# Revit family: Vents_TT PRO EC_2016_19.08
name_source: partatom
category: Оборудование
revit_build: Autodesk Revit 2016 (Build: 20160314_0715(x64)
units: mm (PartAtom-declared; Revit-internal decimal feet)

## family parameters
Всегда вертикально = Нет
На основе рабочей плоскости = Нет
Общий = Нет
При загрузке вырезать с полостями = Нет
Размер круглого соединителя = Использовать диаметр
Тип детали = Вставляется
Точка расчета площади = Нет

## types (7) — shared parameters
CAT0 = Да
CAT1 = Да
CAT2 = Да
Certification = by Manifacturer
EC motor = Да
Ingress Protection Rating = IPX4
LL7 = 98 мм
Motor IP Rating = IPX4
R3 = 49 мм
RR4 = 12 мм
URL = https://ventilation-system.com
Variable Speed Drive = Нет
Voltage = 230 В
W = 500 мм
Группа модели = ТТ PRO EC
Изготовитель = VENTS
Описание = Inline mixed-flow fan
Угол = 60.00°

## per-type parameters (varying)
- TT PRO 160 EC: Current=1 А; D=160 мм; FlowMax=602.0 м³/ч; HH1=50 мм; HH2=49 мм; HH3=109 мм; L8=82 мм; LL1=127 мм; LL2=97 мм; LL3=69 мм; LL4=41 мм; LL6=43 мм; MC Product Code=ТТ PRO 160 EC; Mass=3.25 кг; PC=156 мм; PE=133 мм; Power=65 Вт; R1=79 мм; R2=109 мм; RR3=43 мм; Service Zone=159 мм; Service Zone 1=237 мм; Service Zone 2=254 мм; Sound Pressure Level at 3m  dBA=47; WW1=70 мм; WW2=52 мм
- TT PRO 200 EC: Current=1 А; D=200 мм; FlowMax=1095.0 м³/ч; HH1=50 мм; HH2=49 мм; HH3=120 мм; L8=82 мм; LL1=139 мм; LL2=109 мм; LL3=70 мм; LL4=41 мм; LL6=43 мм; MC Product Code=ТТ PRO 200 EC; Mass=3.95 кг; PC=166 мм; PE=130 мм; Power=140 Вт; R1=99 мм; R2=120 мм; RR3=43 мм; Service Zone=170 мм; Service Zone 1=259 мм; Service Zone 2=278 мм; Sound Pressure Level at 3m  dBA=49; WW1=70 мм; WW2=52 мм
- ТТ PRO 250 EC: Current=1 А; D=250 мм; FlowMax=1500.0 м³/ч; HH1=50 мм; HH2=49 мм; HH3=144 мм; L8=108 мм; LL1=192 мм; LL2=150 мм; LL3=119 мм; LL4=54 мм; LL6=89 мм; MC Product Code=ТТ PRO  250 EC; Mass=7.80 кг; PC=189 мм; PE=150 мм; Power=197 Вт; R1=124 мм; R2=144 мм; RR3=50 мм; Service Zone=194 мм; Service Zone 1=308 мм; Service Zone 2=383 мм; Sound Pressure Level at 3m  dBA=53; WW1=70 мм; WW2=72 мм
- ТТ PRO 315 EC: Current=2 А; D=315 мм; FlowMax=1995.0 м³/ч; HH1=68 мм; HH2=132 мм; HH3=180 мм; L8=108 мм; LL1=222 мм; LL2=192 мм; LL3=155 мм; LL4=54 мм; LL6=118 мм; MC Product Code=ТТ PRO  315 EC; Mass=11.95 кг; PC=223 мм; PE=200 мм; Power=306 Вт; R1=155 мм; R2=180 мм; RR3=50 мм; Service Zone=230 мм; Service Zone 1=380 мм; Service Zone 2=443 мм; Sound Pressure Level at 3m  dBA=55; WW1=100 мм; WW2=102 мм
- TT PRO 150 EC: Current=1 А; D=150 мм; FlowMax=602.0 м³/ч; HH1=68 мм; HH2=132 мм; HH3=109 мм; L8=108 мм; LL1=127 мм; LL2=97 мм; LL3=71 мм; LL4=54 мм; LL6=118 мм; MC Product Code=ТТ PRO 150 EC; Mass=2.95 кг; PC=156 мм; PE=133 мм; Power=65 Вт; R1=74 мм; R2=109 мм; RR3=50 мм; Service Zone=159 мм; Service Zone 1=237 мм; Service Zone 2=254 мм; Sound Pressure Level at 3m  dBA=47; WW1=56 мм; WW2=58 мм
- TT PRO 125 EC: Current=0 А; D=125 мм; FlowMax=460.0 м³/ч; HH1=50 мм; HH2=49 мм; HH3=97 мм; L8=82 мм; LL1=130 мм; LL2=100 мм; LL3=67 мм; LL4=41 мм; LL6=43 мм; MC Product Code=ТТ PRO 125 EC; Mass=2.15 кг; PC=121 мм; PE=120 мм; Power=45 Вт; R1=62 мм; R2=97 мм; RR3=31 мм; Service Zone=147 мм; Service Zone 1=213 мм; Service Zone 2=259 мм; Sound Pressure Level at 3m  dBA=52; WW1=50 мм; WW2=52 мм
- TT PRO 100 EC: Current=0 А; D=100 мм; FlowMax=300.0 м³/ч; HH1=50 мм; HH2=49 мм; HH3=96 мм; L8=82 мм; LL1=152 мм; LL2=124 мм; LL3=65 мм; LL4=41 мм; LL6=43 мм; MC Product Code=ТТ PRO 100 EC; Mass=1.75 кг; PC=120 мм; PE=103 мм; Power=32 Вт; R1=49 мм; R2=96 мм; RR3=31 мм; Service Zone=146 мм; Service Zone 1=212 мм; Service Zone 2=303 мм; Sound Pressure Level at 3m  dBA=47; WW1=50 мм; WW2=52 мм

## geometry (parser evidence)
native form markers: Blend x4, Sweep x2
no freeform markers — native parametric forms only
